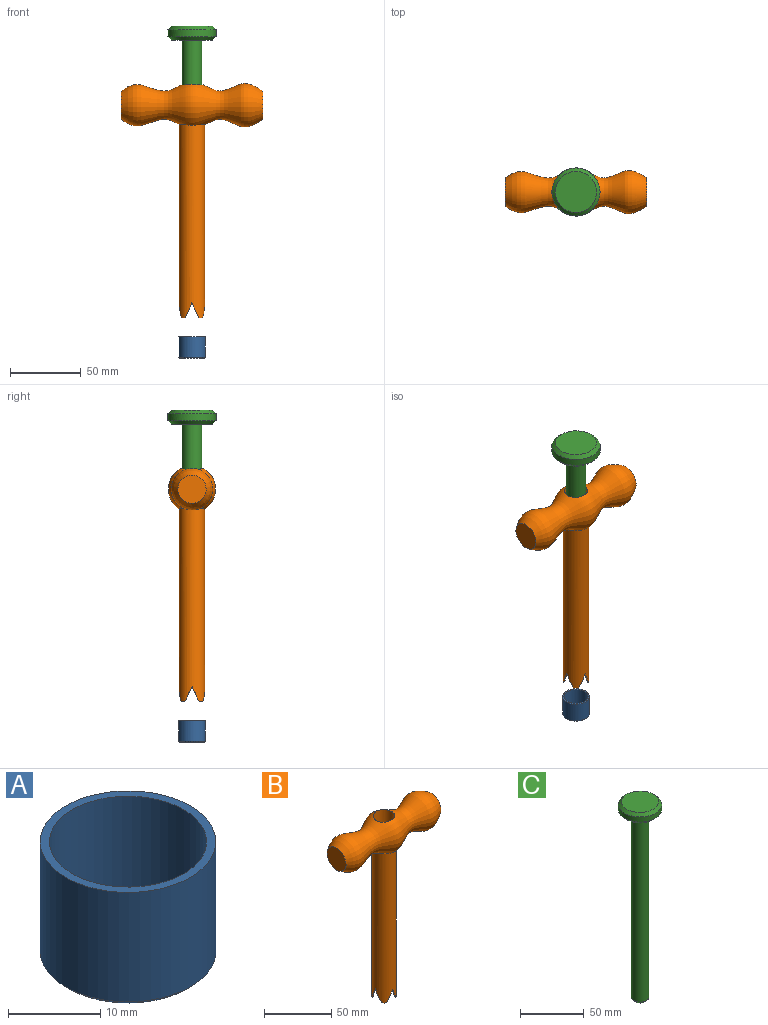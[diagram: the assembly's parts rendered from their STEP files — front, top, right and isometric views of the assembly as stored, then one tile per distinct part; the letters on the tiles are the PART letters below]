
ASSEMBLY  parts=3 mates=2
PART A: 6 faces, bbox 19x19x15 mm
  f0: plane 18x18mm, normal (0,0,-1), area 254.5mm2, adj f5
  f1: cylinder r=9.5mm len=19mm, axis (0,0,1), area 865.5mm2, adj f2,f5
  f2: plane 19x19mm, normal (0,0,1), area 56.5mm2, adj f1,f3
  f3: cylinder r=8.5mm len=17mm, axis (0,0,1), area 747.7mm2, adj f2,f4
  f4: plane 17x17mm, normal (0,0,1), area 227mm2, adj f3
  f5: cone r=9.5mm half-angle=45deg, axis (0,0,1), area 41.1mm2, adj f0,f1
PART B: 21 faces, bbox 100x33.4x166.7 mm
  f0: cylinder r=9mm len=136.48mm, axis (0,0,1), area 7490.5mm2, adj f1,f3,f4,f5,f8,f9,f10,f11
  f1: plane 2.73x2.66mm, normal (0,0,-1), area 1.7mm2, adj f0,f10,f15,f18
  f2: cylinder r=8mm len=164.18mm, axis (0,0,-1), area 8040mm2, adj f5,f9,f10,f11,f12,f13,f14,f15
  f3: plane 2.73x2.66mm, normal (0,0,-1), area 1.7mm2, adj f0,f9,f14,f20
  f4: plane 2.73x2.66mm, normal (0,0,-1), area 1.7mm2, adj f0,f11,f16,f19
  f5: revolved ~100x33.42mm, area -5280.9mm2, adj f0,f2,f6,f7
  f6: plane 20x20mm, normal (1,0,0), area 314.2mm2, adj f5
  f7: plane 20x20mm, normal (-1,0,0), area 314.2mm2, adj f5
  f8: plane 2.73x2.66mm, normal (0,0,-1), area 1.7mm2, adj f0,f12,f13,f17
  f9: plane 10.49x4.77mm, normal (0.91,0,-0.41), area 12.1mm2, adj f0,f2,f3,f10,f20
  f10: plane 10.49x4.77mm, normal (-0.91,0,-0.41), area 12.1mm2, adj f0,f1,f2,f9,f18
  f11: plane 10.49x4.77mm, normal (-0.91,0,-0.41), area 12.1mm2, adj f0,f2,f4,f12,f19
  f12: plane 10.49x4.77mm, normal (0.91,0,-0.41), area 12.1mm2, adj f0,f2,f8,f11,f17
  f13: plane 10.94x4.98mm, normal (0,0.91,-0.41), area 12.7mm2, adj f0,f2,f8,f14,f17
  f14: plane 10.94x4.98mm, normal (0,-0.91,-0.41), area 12.7mm2, adj f0,f2,f3,f13,f20
  f15: plane 10.94x4.98mm, normal (0,-0.91,-0.41), area 12.7mm2, adj f0,f1,f2,f16,f18
  f16: plane 10.94x4.98mm, normal (0,0.91,-0.41), area 12.7mm2, adj f0,f2,f4,f15,f19
  f17: cone r=8.5mm half-angle=45deg, axis (0,0,-1), area 2mm2, adj f2,f8,f12,f13
  f18: cone r=8.5mm half-angle=45deg, axis (0,0,-1), area 2mm2, adj f1,f2,f10,f15
  f19: cone r=8.5mm half-angle=45deg, axis (0,0,-1), area 2mm2, adj f2,f4,f11,f16
  f20: cone r=8.5mm half-angle=45deg, axis (0,0,-1), area 2mm2, adj f2,f3,f9,f14
PART C: 8 faces, bbox 34x34x190 mm
  f0: plane 8x8mm, normal (0,0,-1), area 50.3mm2, adj f7
  f1: cylinder r=7mm len=177mm, axis (0,0,1), area 7784.9mm2, adj f2,f7
  f2: plane 29x29mm, normal (0,0,-1), area 506.6mm2, adj f1,f5
  f3: cylinder r=17mm len=34mm, axis (0,0,1), area 534.1mm2, adj f5,f6
  f4: plane 29x29mm, normal (0,0,1), area 660.5mm2, adj f6
  f5: cone r=17mm half-angle=45deg, axis (0,0,1), area 349.9mm2, adj f2,f3
  f6: cone r=14.5mm half-angle=45deg, axis (0,0,-1), area 349.9mm2, adj f3,f4
  f7: cone r=7mm half-angle=45deg, axis (0,0,1), area 146.6mm2, adj f0,f1
PLACE A t=(74.13,-11.26,-200.84)mm
PLACE B t=(74.13,-11.26,-22.38)mm
PLACE C t=(74.13,-11.26,-156.44)mm
MATE cylindrical A.f1 <-> B.f2  axis (0,0,1) through (74.13,-11.26,-185.84)mm
MATE cylindrical C.f1 <-> B.f0  axis (0,0,1) through (74.13,-11.26,-64.94)mm
